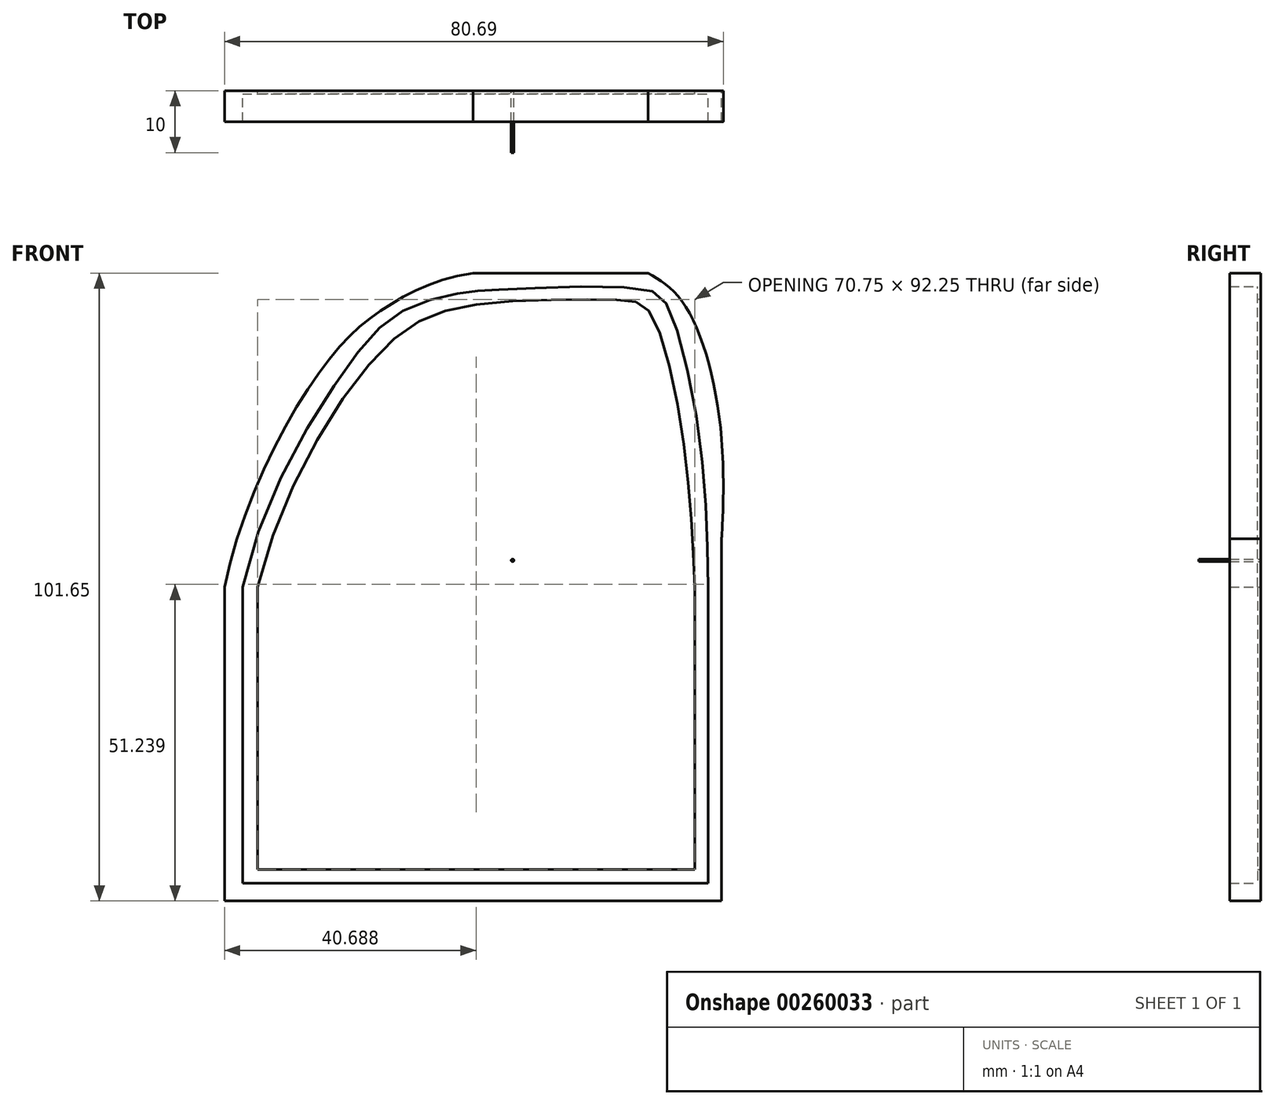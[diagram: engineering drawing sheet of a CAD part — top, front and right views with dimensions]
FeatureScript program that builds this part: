
annotation { "Feature Type Name" : "Feature", "Feature Type Description" : "" }
export const myFeature = defineFeature(function(context is Context, id is Id, definition is map)
    precondition{}
    {
        {
            var Q0;
            Q0=qCreatedBy(makeId("Front.planeOp"),FACE);
            var sketch = newSketch(context, id + "F0", { "sketchPlane" : qUnion([Q0])});
            skCircle(sketch, "E0", {"center": v(0, 0) * mm, "radius": 0.21 * mm});
            skSolve(sketch);
        }
        {
            var Q0;
            Q0 = qSketchRegion(id + "F0", true);
            extrude(context, id + "F1", {"entities" : qUnion([Q0]), "depth" : 10 * mm});
        }
        {
            var Q0;
            Q0=qCreatedBy(makeId("Front.planeOp"),FACE);
            var sketch = newSketch(context, id + "F2", { "sketchPlane" : qUnion([Q0])});
            skLineSegment(sketch, "E1.bottom", {"start": v(-6.38, 46.5) * mm, "end": v(21.95, 46.5) * mm});
            skLineSegment(sketch, "E1.top", {"start": v(-46.59, -55.14) * mm, "end": v(33.83, -55.14) * mm});
            skLineSegment(sketch, "E1.left", {"start": v(-46.59, -4.32) * mm, "end": v(-46.59, -55.14) * mm});
            skLineSegment(sketch, "E1.right", {"start": v(33.83, 19.6) * mm, "end": v(33.83, -55.14) * mm});
            skFitSpline(sketch, "E2", {"points": [v(-46.59, -4.32) * mm, v(-30.87, 31) * mm, v(-20.25, 41.13) * mm, v(-6.38, 46.5) * mm], "startDerivative": vector(17.33, 88.44) * mm, "endDerivative": vector(60.56, 8.43) * mm});
            skPoint(sketch, "E3.orphan", {"position": v(-46.59, 46.5) * mm});
            skFitSpline(sketch, "E4", {"points": [v(21.95, 46.5) * mm, v(27.63, 41.64) * mm, v(33.83, 19.6) * mm, v(33.83, 3.49) * mm, v(33.83, 3.37) * mm], "startDerivative": vector(25.35, -15.2) * mm, "endDerivative": vector(0.18, -3.1) * mm});
            skPoint(sketch, "E5.orphan", {"position": v(33.83, 46.5) * mm});
            skLineSegment(sketch, "E6.top", {"start": v(-43.68, -52.26) * mm, "end": v(31.62, -52.26) * mm});
            skLineSegment(sketch, "E6.left", {"start": v(-43.68, -4.32) * mm, "end": v(-43.68, -52.26) * mm});
            skLineSegment(sketch, "E6.right", {"start": v(31.62, -4.32) * mm, "end": v(31.62, -52.26) * mm});
            skFitSpline(sketch, "E7", {"points": [v(-43.68, -4.32) * mm, v(-27, 31) * mm, v(-17.27, 40.65) * mm, v(-7.5, 43.38) * mm, v(-1.6, 43.84) * mm, v(20.74, 44) * mm, v(25.12, 41.13) * mm, v(30.28, 19.6) * mm, v(31.62, -4.32) * mm], "startDerivative": vector(40.76, 206.76) * mm, "endDerivative": vector(0.55, -146.46) * mm});
            skLineSegment(sketch, "E8.top", {"start": v(-41.28, -50.03) * mm, "end": v(29.47, -50.03) * mm});
            skLineSegment(sketch, "E8.left", {"start": v(-41.28, -4.32) * mm, "end": v(-41.28, -50.03) * mm});
            skLineSegment(sketch, "E8.right", {"start": v(29.47, -4.32) * mm, "end": v(29.47, -50.03) * mm});
            skFitSpline(sketch, "E9", {"points": [v(29.47, -4.32) * mm, v(27.6, 19.6) * mm, v(21.96, 40.45) * mm, v(16.9, 42.14) * mm, v(-5.95, 41.4) * mm, v(-20.95, 34.2) * mm, v(-41.28, -4.32) * mm], "startDerivative": vector(-5.83, 122.07) * mm, "endDerivative": vector(-47.07, -192.85) * mm});
            skSolve(sketch);
        }
        {
            var Q0;
            Q0 = qSketchRegion(id + "F2", true);
            extrude(context, id + "F3", {"entities" : qUnion([Q0]), "depth" : 5 * mm});
        }
        {
            var Q0;
            Q0=makeQuery(id+"F2.imprint","IMPRINT",FACE,{"disambiguationData":[TD([[makeQuery(id+"F2.imprint","IMPRINT",EDGE,{"derivedFrom":sQuery(id+"F2.wireOp",EDGE,"E6.top")}),1.0]])]});
            extrude(context, id + "F4", {"entities" : qUnion([Q0]), "operationType" : NewBodyOperationType.ADD, "depth" : 0.5 * mm});
        }
    });
